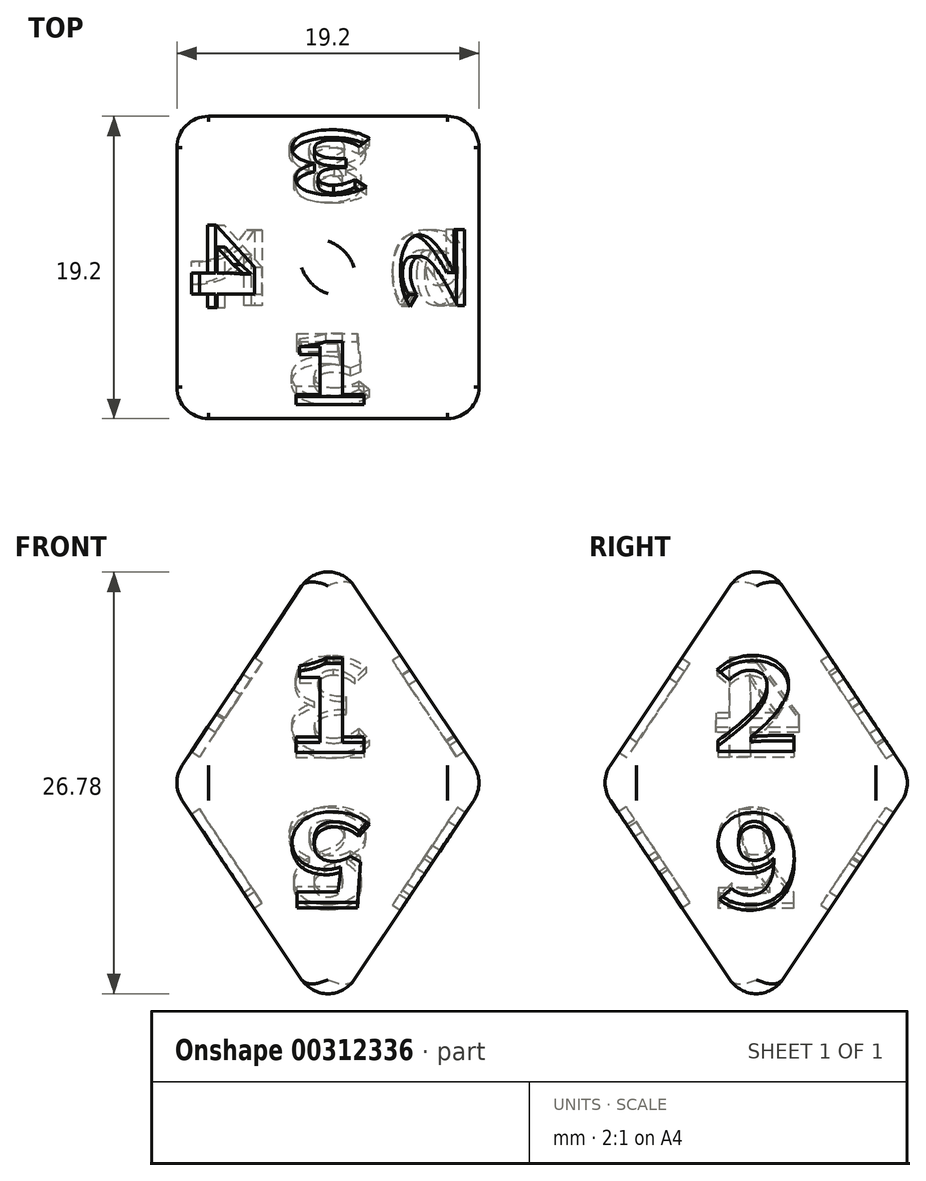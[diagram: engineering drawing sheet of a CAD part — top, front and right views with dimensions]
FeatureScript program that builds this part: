
annotation { "Feature Type Name" : "Feature", "Feature Type Description" : "" }
export const myFeature = defineFeature(function(context is Context, id is Id, definition is map)
    precondition{}
    {
        {
            var Q0;
            Q0=qCreatedBy(makeId("Top.planeOp"),FACE);
            var sketch = newSketch(context, id + "F0", { "sketchPlane" : qUnion([Q0])});
            skLineSegment(sketch, "E0.bottom", {"start": v(10, 10) * mm, "end": v(-10, 10) * mm});
            skLineSegment(sketch, "E0.top", {"start": v(10, -10) * mm, "end": v(-10, -10) * mm});
            skLineSegment(sketch, "E0.left", {"start": v(10, 10) * mm, "end": v(10, -10) * mm});
            skLineSegment(sketch, "E0.right", {"start": v(-10, 10) * mm, "end": v(-10, -10) * mm});
            skPoint(sketch, "E0.middle", {"position": v(0, 0) * mm});
            skSolve(sketch);
        }
        {
            var Q0;
            Q0 = qSketchRegion(id + "F0", true);
            extrude(context, id + "F1", {"entities" : qUnion([Q0]), "depth" : 15 * mm});
        }
        {
            var Q0;
            Q0=makeQuery(id+"F1.opExtrude","CAP_FACE",FACE,{"disambiguationData":[OSD([sQuery(id+"F0.wireOp",EDGE,"E0.bottom"),sQuery(id+"F0.wireOp",EDGE,"E0.top"),sQuery(id+"F0.wireOp",EDGE,"E0.left"),sQuery(id+"F0.wireOp",EDGE,"E0.right")])],"isStart":true});
            extrude(context, id + "F2", {"entities" : qUnion([Q0]), "depth" : 15 * mm});
        }
        {
            var Q0;
            Q0=makeQuery(id+"F2.opExtrude","CAP_FACE",FACE,{"disambiguationData":[OSD([sQuery(id+"F0.wireOp",EDGE,"E0.bottom"),sQuery(id+"F0.wireOp",EDGE,"E0.top"),sQuery(id+"F0.wireOp",EDGE,"E0.left"),sQuery(id+"F0.wireOp",EDGE,"E0.right")])],"isStart":false});
            chamfer(context, id + "F3", {"entities" : qUnion([Q0]), "chamferType" : ChamferType.TWO_OFFSETS, "width1" : 15 * mm, "oppositeDirection" : false, "width2" : 10 * mm, "tangentPropagation" : true});
        }
        {
            var Q0;
            Q0=makeQuery(id+"F1.opExtrude","CAP_FACE",FACE,{"disambiguationData":[OSD([sQuery(id+"F0.wireOp",EDGE,"E0.bottom"),sQuery(id+"F0.wireOp",EDGE,"E0.top"),sQuery(id+"F0.wireOp",EDGE,"E0.left"),sQuery(id+"F0.wireOp",EDGE,"E0.right")])],"isStart":false});
            chamfer(context, id + "F4", {"entities" : qUnion([Q0]), "chamferType" : ChamferType.TWO_OFFSETS, "width1" : 10 * mm, "oppositeDirection" : false, "width2" : 15 * mm, "tangentPropagation" : true});
        }
        {
            var Q0;
            Q0=makeQuery(id+"F2.opExtrude","SWEPT_BODY",BODY,{"disambiguationData":[OSD([sQuery(id+"F0.wireOp",EDGE,"E0.bottom"),sQuery(id+"F0.wireOp",EDGE,"E0.top"),sQuery(id+"F0.wireOp",EDGE,"E0.left"),sQuery(id+"F0.wireOp",EDGE,"E0.right")])]});
            var Q1;
            Q1=makeQuery(id+"F1.opExtrude","SWEPT_BODY",BODY,{"disambiguationData":[OSD([sQuery(id+"F0.wireOp",EDGE,"E0.bottom"),sQuery(id+"F0.wireOp",EDGE,"E0.top"),sQuery(id+"F0.wireOp",EDGE,"E0.left"),sQuery(id+"F0.wireOp",EDGE,"E0.right")])]});
            booleanBodies(context, id + "F5", {"operationType" : BooleanOperationType.UNION, "tools" : qUnion([Q0, Q1])});
        }
        {
            var Q0;
            Q0=makeQuery(id+"F4.opChamfer","BLEND_FACE",FACE,{"disambiguationData":[OSD([sQuery(id+"F0.wireOp",EDGE,"E0.left")])]});
            var Q1;
            Q1=makeQuery(id+"F3.opChamfer","BLEND_FACE",FACE,{"disambiguationData":[OSD([sQuery(id+"F0.wireOp",EDGE,"E0.bottom")])]});
            var Q2;
            Q2=makeQuery(id+"F3.opChamfer","BLEND_FACE",FACE,{"disambiguationData":[OSD([sQuery(id+"F0.wireOp",EDGE,"E0.top")])]});
            var Q3;
            Q3=makeQuery(id+"F4.opChamfer","BLEND_FACE",FACE,{"disambiguationData":[OSD([sQuery(id+"F0.wireOp",EDGE,"E0.right")])]});
            fillet(context, id + "F6", {"entities" : qUnion([Q0, Q1, Q2, Q3]), "radius" : 2 * mm, "tangentPropagation" : true, "allowEdgeOverflow" : false});
        }
        {
            var Q0;
            Q0=makeQuery(id+"F4.opChamfer","BLEND_FACE",FACE,{"disambiguationData":[OSD([sQuery(id+"F0.wireOp",EDGE,"E0.top")])]});
            var sketch = newSketch(context, id + "F7", { "sketchPlane" : qUnion([Q0])});
            skText(sketch, "E1", { "text": "1", "fontName": "NotoSansCJKtc-Bold.otf"});
            skPoint(sketch, "E2", {"position": v(0, 0.29) * mm});
            const initialGuessF7  = {"E1": [-0.00284, -0.00321, 1, 0, 0.007]};
            skSetInitialGuess(sketch, initialGuessF7);
            skSolve(sketch);
        }
        {
            var Q0;
            Q0=makeQuery(id+"F4.opChamfer","BLEND_FACE",FACE,{"disambiguationData":[OSD([sQuery(id+"F0.wireOp",EDGE,"E0.left")])]});
            var sketch = newSketch(context, id + "F8", { "sketchPlane" : qUnion([Q0])});
            skText(sketch, "E3", { "text": "2", "fontName": "NotoSansCJKtc-Bold.otf"});
            skPoint(sketch, "E4", {"position": v(0.06, 0.35) * mm});
            const initialGuessF8  = {"E3": [-0.00284, -0.00315, 1, 0, 0.007]};
            skSetInitialGuess(sketch, initialGuessF8);
            skSolve(sketch);
        }
        {
            var Q0;
            Q0=makeQuery(id+"F4.opChamfer","BLEND_FACE",FACE,{"disambiguationData":[OSD([sQuery(id+"F0.wireOp",EDGE,"E0.bottom")])]});
            var sketch = newSketch(context, id + "F9", { "sketchPlane" : qUnion([Q0])});
            skText(sketch, "E5", { "text": "3", "fontName": "NotoSansCJKtc-Bold.otf"});
            skPoint(sketch, "E6", {"position": v(-0.02, 0.35) * mm});
            const initialGuessF9  = {"E5": [-0.0029, -0.00315, 1, 0, 0.007]};
            skSetInitialGuess(sketch, initialGuessF9);
            skSolve(sketch);
        }
        {
            var Q0;
            Q0=makeQuery(id+"F4.opChamfer","BLEND_FACE",FACE,{"disambiguationData":[OSD([sQuery(id+"F0.wireOp",EDGE,"E0.right")])]});
            var sketch = newSketch(context, id + "F10", { "sketchPlane" : qUnion([Q0])});
            skText(sketch, "E7", { "text": "4", "fontName": "NotoSansCJKtc-Bold.otf"});
            skPoint(sketch, "E8", {"position": v(0.1, 0.35) * mm});
            const initialGuessF10  = {"E7": [-0.0029, -0.00315, 1, 0, 0.007]};
            skSetInitialGuess(sketch, initialGuessF10);
            skSolve(sketch);
        }
        {
            var Q0;
            Q0=makeQuery(id+"F3.opChamfer","BLEND_FACE",FACE,{"disambiguationData":[OSD([sQuery(id+"F0.wireOp",EDGE,"E0.top")])]});
            var sketch = newSketch(context, id + "F11", { "sketchPlane" : qUnion([Q0])});
            skText(sketch, "E9", { "text": "5", "fontName": "NotoSansCJKtc-Bold.otf"});
            skPoint(sketch, "E10", {"position": v(0, -0.29) * mm});
            const initialGuessF11  = {"E9": [0.0029, 0.00321, -1, 0, 0.007]};
            skSetInitialGuess(sketch, initialGuessF11);
            skSolve(sketch);
        }
        {
            var Q0;
            Q0=makeQuery(id+"F3.opChamfer","BLEND_FACE",FACE,{"disambiguationData":[OSD([sQuery(id+"F0.wireOp",EDGE,"E0.left")])]});
            var sketch = newSketch(context, id + "F12", { "sketchPlane" : qUnion([Q0])});
            skText(sketch, "E11", { "text": "6", "fontName": "NotoSansCJKtc-Bold.otf"});
            skPoint(sketch, "E12", {"position": v(0, -0.35) * mm});
            const initialGuessF12  = {"E11": [0.0029, 0.00315, -1, 0, 0.007]};
            skSetInitialGuess(sketch, initialGuessF12);
            skSolve(sketch);
        }
        {
            var Q0;
            Q0=makeQuery(id+"F3.opChamfer","BLEND_FACE",FACE,{"disambiguationData":[OSD([sQuery(id+"F0.wireOp",EDGE,"E0.right")])]});
            var sketch = newSketch(context, id + "F13", { "sketchPlane" : qUnion([Q0])});
            skText(sketch, "E13", { "text": "7", "fontName": "NotoSansCJKtc-Bold.otf"});
            skPoint(sketch, "E14", {"position": v(0, -0.35) * mm});
            const initialGuessF13  = {"E13": [0.0029, 0.00315, -1, 0, 0.007]};
            skSetInitialGuess(sketch, initialGuessF13);
            skSolve(sketch);
        }
        {
            var Q0;
            Q0=makeQuery(id+"F3.opChamfer","BLEND_FACE",FACE,{"disambiguationData":[OSD([sQuery(id+"F0.wireOp",EDGE,"E0.bottom")])]});
            var sketch = newSketch(context, id + "F14", { "sketchPlane" : qUnion([Q0])});
            skText(sketch, "E15", { "text": "8\n", "fontName": "NotoSansCJKtc-Bold.otf"});
            skPoint(sketch, "E16", {"position": v(0, -0.35) * mm});
            const initialGuessF14  = {"E15": [0.0029, 0.00315, -1, 0, 0.007]};
            skSetInitialGuess(sketch, initialGuessF14);
            skSolve(sketch);
        }
        {
            var Q0;
            Q0 = qSketchRegion(id + "F7", true);
            var Q1;
            Q1=makeQuery(id+"F14.imprint","IMPRINT",FACE,{"disambiguationData":[TD([[makeQuery(id+"F14.imprint","IMPRINT",EDGE,{"derivedFrom":sQuery(id+"F14.wireOp",EDGE,"E15.sketch_text.stroke-0")}),1.0]])]});
            extrude(context, id + "F15", {"entities" : qUnion([Q0, Q1]), "operationType" : NewBodyOperationType.REMOVE, "depth" : 0.6 * mm, "hasSecondDirection" : true, "secondDirectionOppositeDirection" : true, "secondDirectionDepth" : 0.6 * mm});
        }
        {
            var Q0;
            Q0=makeQuery(id+"F13.imprint","IMPRINT",FACE,{"disambiguationData":[TD([[makeQuery(id+"F13.imprint","IMPRINT",EDGE,{"derivedFrom":sQuery(id+"F13.wireOp",EDGE,"E13.sketch_text.stroke-0")}),1.0]])]});
            var Q1;
            Q1=makeQuery(id+"F8.imprint","IMPRINT",FACE,{"disambiguationData":[TD([[makeQuery(id+"F8.imprint","IMPRINT",EDGE,{"derivedFrom":sQuery(id+"F8.wireOp",EDGE,"E3.sketch_text.stroke-0")}),1.0]])]});
            extrude(context, id + "F16", {"entities" : qUnion([Q0, Q1]), "operationType" : NewBodyOperationType.REMOVE, "oppositeDirection" : true, "depth" : 0.6 * mm, "hasSecondDirection" : true, "secondDirectionOppositeDirection" : false, "secondDirectionDepth" : 0.6 * mm});
        }
        {
            var Q0;
            Q0=makeQuery(id+"F9.imprint","IMPRINT",FACE,{"disambiguationData":[TD([[makeQuery(id+"F9.imprint","IMPRINT",EDGE,{"derivedFrom":sQuery(id+"F9.wireOp",EDGE,"E5.sketch_text.stroke-0")}),1.0]])]});
            var Q1;
            Q1=makeQuery(id+"F11.imprint","IMPRINT",FACE,{"disambiguationData":[TD([[makeQuery(id+"F11.imprint","IMPRINT",EDGE,{"derivedFrom":sQuery(id+"F11.wireOp",EDGE,"E9.sketch_text.stroke-0")}),1.0]])]});
            extrude(context, id + "F17", {"entities" : qUnion([Q0, Q1]), "operationType" : NewBodyOperationType.REMOVE, "oppositeDirection" : true, "depth" : 0.6 * mm, "hasSecondDirection" : true, "secondDirectionOppositeDirection" : false, "secondDirectionDepth" : 0.6 * mm});
        }
        {
            var Q0;
            Q0=makeQuery(id+"F12.imprint","IMPRINT",FACE,{"disambiguationData":[TD([[makeQuery(id+"F12.imprint","IMPRINT",EDGE,{"derivedFrom":sQuery(id+"F12.wireOp",EDGE,"E11.sketch_text.stroke-0")}),1.0]])]});
            var Q1;
            Q1=makeQuery(id+"F10.imprint","IMPRINT",FACE,{"disambiguationData":[TD([[makeQuery(id+"F10.imprint","IMPRINT",EDGE,{"derivedFrom":sQuery(id+"F10.wireOp",EDGE,"E7.sketch_text.stroke-0")}),1.0]])]});
            extrude(context, id + "F18", {"entities" : qUnion([Q0, Q1]), "operationType" : NewBodyOperationType.REMOVE, "oppositeDirection" : true, "depth" : 0.6 * mm, "hasSecondDirection" : true, "secondDirectionOppositeDirection" : false, "secondDirectionDepth" : 0.6 * mm});
        }
    });
